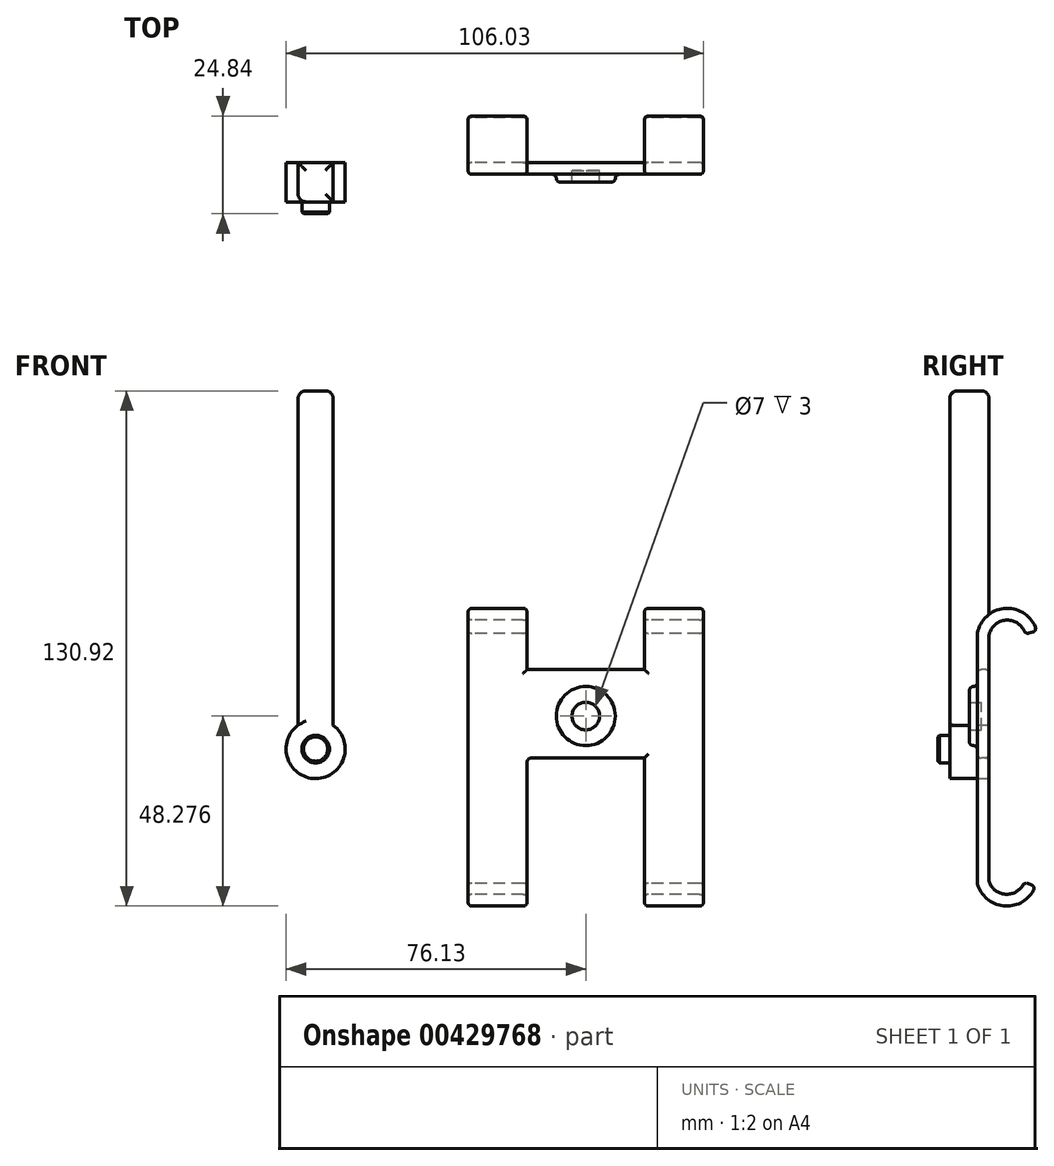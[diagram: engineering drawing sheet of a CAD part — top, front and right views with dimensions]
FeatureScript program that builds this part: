
annotation { "Feature Type Name" : "Feature", "Feature Type Description" : "" }
export const myFeature = defineFeature(function(context is Context, id is Id, definition is map)
    precondition{}
    {
        {
            var Q0;
            Q0=qCreatedBy(makeId("Right.planeOp"),FACE);
            var sketch = newSketch(context, id + "F0", { "sketchPlane" : qUnion([Q0])});
            skLineSegment(sketch, "E0", {"start": v(0, 2.96) * mm, "end": v(0, 65.68) * mm});
            skArc(sketch, "E1", {"start": v(9.23, 65.81) * mm, "mid": v(4.56, 69.36) * mm, "end": v(0, 65.68) * mm});
            skArc(sketch, "E2", {"start": v(0, 2.96) * mm, "mid": v(4.42, -0.3) * mm, "end": v(8.96, 2.78) * mm});
            skPoint(sketch, "E3.orphan", {"position": v(0, 0) * mm});
            skArc(sketch, "E4.0", {"start": v(-3, 2.53) * mm, "mid": v(4.09, -3.29) * mm, "end": v(11.77, 1.72) * mm});
            skLineSegment(sketch, "E4.1", {"start": v(-3, 2.53) * mm, "end": v(-3, 65.99) * mm});
            skArc(sketch, "E4.2", {"start": v(12.13, 66.57) * mm, "mid": v(4.33, 72.35) * mm, "end": v(-3, 65.99) * mm});
            skLineSegment(sketch, "E5", {"start": v(11.77, 1.72) * mm, "end": v(8.96, 2.78) * mm});
            skLineSegment(sketch, "E6", {"start": v(12.13, 66.57) * mm, "end": v(9.23, 65.81) * mm});
            skSolve(sketch);
        }
        {
            var Q0;
            Q0=makeQuery(id+"F0.imprint","IMPRINT",FACE,{"disambiguationData":[TD([[makeQuery(id+"F0.imprint","IMPRINT",EDGE,{"derivedFrom":sQuery(id+"F0.wireOp",EDGE,"E0")}),1.0]])]});
            extrude(context, id + "F1", {"entities" : qUnion([Q0]), "depth" : 15 * mm});
        }
        {
            var Q0;
            Q0=makeQuery(id+"F1.opExtrude","SWEPT_BODY",BODY,{"disambiguationData":[OSD([sQuery(id+"F0.wireOp",EDGE,"E0"),sQuery(id+"F0.wireOp",EDGE,"E1"),sQuery(id+"F0.wireOp",EDGE,"E2"),sQuery(id+"F0.wireOp",EDGE,"E4.0"),sQuery(id+"F0.wireOp",EDGE,"E4.1"),sQuery(id+"F0.wireOp",EDGE,"E4.2"),sQuery(id+"F0.wireOp",EDGE,"E5"),sQuery(id+"F0.wireOp",EDGE,"E6")])]});
            transform(context, id + "F2", {"entities" : qUnion([Q0]), "transformType" : TransformType.TRANSLATION_3D, "dx" : 44.8 * mm, "dy" : 0 * mm, "dz" : 0 * mm, "makeCopy" : true});
        }
        {
            var Q0;
            Q0=makeQuery(id+"F1.opExtrude","CAP_FACE",FACE,{"disambiguationData":[OSD([sQuery(id+"F0.wireOp",EDGE,"E0"),sQuery(id+"F0.wireOp",EDGE,"E1"),sQuery(id+"F0.wireOp",EDGE,"E2"),sQuery(id+"F0.wireOp",EDGE,"E4.0"),sQuery(id+"F0.wireOp",EDGE,"E4.1"),sQuery(id+"F0.wireOp",EDGE,"E4.2"),sQuery(id+"F0.wireOp",EDGE,"E5"),sQuery(id+"F0.wireOp",EDGE,"E6")])],"isStart":false});
            var sketch = newSketch(context, id + "F3", { "sketchPlane" : qUnion([Q0])});
            skLineSegment(sketch, "E7", {"start": v(0, 34.32) * mm, "end": v(-3, 34.32) * mm});
            skLineSegment(sketch, "E8", {"start": v(0, 56.8) * mm, "end": v(-3, 56.8) * mm});
            skSolve(sketch);
        }
        {
            var Q0;
            {var subQ0=sQuery(id+"F3.wireOp",EDGE,"E7");Q0=makeQuery(id+"F3.imprint","IMPRINT",FACE,{"disambiguationData":[TD([[makeQuery(id+"F3.imprint","IMPRINT",EDGE,{"derivedFrom":subQ0}),-1.0]])]});}
            extrude(context, id + "F4", {"entities" : qUnion([Q0]), "operationType" : NewBodyOperationType.ADD, "endBound" : BoundingType.UP_TO_NEXT, "depth" : 25 * mm});
        }
        {
            var Q0;
            {var subQ0=sQuery(id+"F0.wireOp",EDGE,"E4.1");var subQ1=makeQuery(id+"F1.opExtrude","SWEPT_FACE",FACE,{"disambiguationData":[OSD([subQ0])]});Q0=makeQuery(id+"F4.boolean.opBoolean","MERGE",FACE,{"derivedFrom":[subQ1,makeQuery(id+"F2.opPattern","COPY",FACE,{"derivedFrom":subQ1,"instanceName":"1"}),makeQuery(id+"F4.opExtrude","SWEPT_FACE",FACE,{"disambiguationData":[OSD([subQ0])]})]});}
            var sketch = newSketch(context, id + "F5", { "sketchPlane" : qUnion([Q0])});
            skCircle(sketch, "E9", {"center": v(29.9, 44.98) * mm, "radius": 7.5 * mm});
            skCircle(sketch, "E10", {"center": v(29.9, 44.98) * mm, "radius": 3.5 * mm});
            skSolve(sketch);
        }
        {
            var Q0;
            Q0 = qSketchRegion(id + "F5", true);
            extrude(context, id + "F6", {"entities" : qUnion([Q0]), "operationType" : NewBodyOperationType.ADD, "depth" : 2 * mm});
        }
        {
            var Q0;
            Q0=makeQuery(id+"F6.opExtrude","CAP_EDGE",EDGE,{"disambiguationData":[OSD([sQuery(id+"F5.wireOp",EDGE,"E9")])],"isStart":false});
            var Q1;
            Q1=makeQuery(id+"F4.opExtrude","SWEPT_EDGE",EDGE,{"disambiguationData":[OSD([sQuery(id+"F0.wireOp",EDGE,"E4.1"),sQuery(id+"F3.wireOp",EDGE,"E8")])]});
            var Q2;
            Q2=makeQuery(id+"F4.opExtrude","SWEPT_EDGE",EDGE,{"disambiguationData":[OSD([sQuery(id+"F0.wireOp",EDGE,"E4.1"),sQuery(id+"F3.wireOp",EDGE,"E7")])]});
            var Q3;
            {var subQ0=sQuery(id+"F0.wireOp",EDGE,"E4.1");var subQ2=sQuery(id+"F0.wireOp",EDGE,"E4.0");Q3=makeQuery(id+"F4.boolean.opBoolean","SPLIT",EDGE,{"disambiguationData":[TD([makeQuery(id+"F1.opExtrude","SWEPT_FACE",FACE,{"disambiguationData":[OSD([subQ2])]})])],"derivedFrom":makeQuery(id+"F1.opExtrude","CAP_EDGE",EDGE,{"disambiguationData":[OSD([subQ0])],"isStart":false})});}
            var Q4;
            {var subQ0=sQuery(id+"F0.wireOp",EDGE,"E4.1");var subQ2=sQuery(id+"F0.wireOp",EDGE,"E4.0");Q4=makeQuery(id+"F4.boolean.opBoolean","SPLIT",EDGE,{"disambiguationData":[TD([makeQuery(id+"F2.opPattern","COPY",FACE,{"derivedFrom":makeQuery(id+"F1.opExtrude","SWEPT_FACE",FACE,{"disambiguationData":[OSD([subQ2])]}),"instanceName":"1"})])],"derivedFrom":makeQuery(id+"F2.opPattern","COPY",EDGE,{"derivedFrom":makeQuery(id+"F1.opExtrude","CAP_EDGE",EDGE,{"disambiguationData":[OSD([subQ0])],"isStart":true}),"instanceName":"1"})});}
            var Q5;
            {var subQ2=sQuery(id+"F0.wireOp",EDGE,"E4.0");var subQ3=makeQuery(id+"F1.opExtrude","SWEPT_FACE",FACE,{"disambiguationData":[OSD([subQ2])]});var subQ6=sQuery(id+"F0.wireOp",EDGE,"E4.1");var subQ12=makeQuery(id+"F1.opExtrude","SWEPT_FACE",FACE,{"disambiguationData":[OSD([subQ6])]});Q5=makeQuery(id+"F6.boolean.opBoolean","SPLIT",FACE,{"disambiguationData":[TD([subQ3])],"derivedFrom":makeQuery(id+"F4.boolean.opBoolean","MERGE",FACE,{"derivedFrom":[subQ12,makeQuery(id+"F2.opPattern","COPY",FACE,{"derivedFrom":subQ12,"instanceName":"1"}),makeQuery(id+"F4.opExtrude","SWEPT_FACE",FACE,{"disambiguationData":[OSD([subQ6])]})]})});}
            var Q6;
            {var subQ0=sQuery(id+"F0.wireOp",EDGE,"E0");var subQ1=makeQuery(id+"F1.opExtrude","SWEPT_FACE",FACE,{"disambiguationData":[OSD([subQ0])]});Q6=makeQuery(id+"F4.boolean.opBoolean","MERGE",FACE,{"derivedFrom":[subQ1,makeQuery(id+"F2.opPattern","COPY",FACE,{"derivedFrom":subQ1,"instanceName":"1"}),makeQuery(id+"F4.opExtrude","SWEPT_FACE",FACE,{"disambiguationData":[OSD([subQ0])]})]});}
            var Q7;
            Q7=makeQuery(id+"F1.opExtrude","SWEPT_FACE",FACE,{"disambiguationData":[OSD([sQuery(id+"F0.wireOp",EDGE,"E4.0")])]});
            var Q8;
            Q8=makeQuery(id+"F1.opExtrude","SWEPT_FACE",FACE,{"disambiguationData":[OSD([sQuery(id+"F0.wireOp",EDGE,"E4.2")])]});
            var Q9;
            Q9=makeQuery(id+"F2.opPattern","COPY",FACE,{"derivedFrom":makeQuery(id+"F1.opExtrude","SWEPT_FACE",FACE,{"disambiguationData":[OSD([sQuery(id+"F0.wireOp",EDGE,"E4.2")])]}),"instanceName":"1"});
            var Q10;
            Q10=makeQuery(id+"F2.opPattern","COPY",EDGE,{"derivedFrom":makeQuery(id+"F1.opExtrude","SWEPT_EDGE",EDGE,{"disambiguationData":[OSD([sQuery(id+"F0.wireOp",EDGE,"E0"),sQuery(id+"F0.wireOp",EDGE,"E2")])]}),"instanceName":"1"});
            var Q11;
            Q11=makeQuery(id+"F2.opPattern","COPY",EDGE,{"derivedFrom":makeQuery(id+"F1.opExtrude","CAP_EDGE",EDGE,{"disambiguationData":[OSD([sQuery(id+"F0.wireOp",EDGE,"E0")])],"isStart":false}),"instanceName":"1"});
            var Q12;
            Q12=makeQuery(id+"F2.opPattern","COPY",EDGE,{"derivedFrom":makeQuery(id+"F1.opExtrude","CAP_EDGE",EDGE,{"disambiguationData":[OSD([sQuery(id+"F0.wireOp",EDGE,"E2")])],"isStart":true}),"instanceName":"1"});
            var Q13;
            Q13=makeQuery(id+"F2.opPattern","COPY",EDGE,{"derivedFrom":makeQuery(id+"F1.opExtrude","SWEPT_EDGE",EDGE,{"disambiguationData":[OSD([sQuery(id+"F0.wireOp",EDGE,"E4.0"),sQuery(id+"F0.wireOp",EDGE,"E5")])]}),"instanceName":"1"});
            var Q14;
            Q14=makeQuery(id+"F2.opPattern","COPY",EDGE,{"derivedFrom":makeQuery(id+"F1.opExtrude","SWEPT_EDGE",EDGE,{"disambiguationData":[OSD([sQuery(id+"F0.wireOp",EDGE,"E2"),sQuery(id+"F0.wireOp",EDGE,"E5")])]}),"instanceName":"1"});
            var Q15;
            {var subQ0=sQuery(id+"F0.wireOp",EDGE,"E2");var subQ1=sQuery(id+"F0.wireOp",EDGE,"E0");Q15=makeQuery(id+"F4.boolean.opBoolean","SPLIT",EDGE,{"disambiguationData":[TD([makeQuery(id+"F2.opPattern","COPY",FACE,{"derivedFrom":makeQuery(id+"F1.opExtrude","SWEPT_FACE",FACE,{"disambiguationData":[OSD([subQ0])]}),"instanceName":"1"})])],"derivedFrom":makeQuery(id+"F2.opPattern","COPY",EDGE,{"derivedFrom":makeQuery(id+"F1.opExtrude","CAP_EDGE",EDGE,{"disambiguationData":[OSD([subQ1])],"isStart":true}),"instanceName":"1"})});}
            var Q16;
            Q16=makeQuery(id+"F2.opPattern","COPY",EDGE,{"derivedFrom":makeQuery(id+"F1.opExtrude","CAP_EDGE",EDGE,{"disambiguationData":[OSD([sQuery(id+"F0.wireOp",EDGE,"E4.0")])],"isStart":true}),"instanceName":"1"});
            var Q17;
            Q17=makeQuery(id+"F2.opPattern","COPY",EDGE,{"derivedFrom":makeQuery(id+"F1.opExtrude","CAP_EDGE",EDGE,{"disambiguationData":[OSD([sQuery(id+"F0.wireOp",EDGE,"E5")])],"isStart":true}),"instanceName":"1"});
            var Q18;
            Q18=makeQuery(id+"F1.opExtrude","SWEPT_EDGE",EDGE,{"disambiguationData":[OSD([sQuery(id+"F0.wireOp",EDGE,"E4.0"),sQuery(id+"F0.wireOp",EDGE,"E5")])]});
            var Q19;
            Q19=makeQuery(id+"F1.opExtrude","SWEPT_EDGE",EDGE,{"disambiguationData":[OSD([sQuery(id+"F0.wireOp",EDGE,"E4.1"),sQuery(id+"F0.wireOp",EDGE,"E4.2")])]});
            var Q20;
            Q20=makeQuery(id+"F1.opExtrude","CAP_EDGE",EDGE,{"disambiguationData":[OSD([sQuery(id+"F0.wireOp",EDGE,"E1")])],"isStart":false});
            var Q21;
            Q21=makeQuery(id+"F2.opPattern","COPY",EDGE,{"derivedFrom":makeQuery(id+"F1.opExtrude","SWEPT_EDGE",EDGE,{"disambiguationData":[OSD([sQuery(id+"F0.wireOp",EDGE,"E4.0"),sQuery(id+"F0.wireOp",EDGE,"E4.1")])]}),"instanceName":"1"});
            var Q22;
            Q22=makeQuery(id+"F2.opPattern","COPY",EDGE,{"derivedFrom":makeQuery(id+"F1.opExtrude","CAP_EDGE",EDGE,{"disambiguationData":[OSD([sQuery(id+"F0.wireOp",EDGE,"E4.0")])],"isStart":false}),"instanceName":"1"});
            var Q23;
            Q23=makeQuery(id+"F4.opExtrude","SWEPT_EDGE",EDGE,{"disambiguationData":[OSD([sQuery(id+"F0.wireOp",EDGE,"E0"),sQuery(id+"F3.wireOp",EDGE,"E7")])]});
            var Q24;
            Q24=makeQuery(id+"F1.opExtrude","SWEPT_EDGE",EDGE,{"disambiguationData":[OSD([sQuery(id+"F0.wireOp",EDGE,"E4.0"),sQuery(id+"F0.wireOp",EDGE,"E4.1")])]});
            var Q25;
            Q25=makeQuery(id+"F1.opExtrude","SWEPT_EDGE",EDGE,{"disambiguationData":[OSD([sQuery(id+"F0.wireOp",EDGE,"E2"),sQuery(id+"F0.wireOp",EDGE,"E5")])]});
            var Q26;
            Q26=makeQuery(id+"F1.opExtrude","CAP_EDGE",EDGE,{"disambiguationData":[OSD([sQuery(id+"F0.wireOp",EDGE,"E2")])],"isStart":false});
            var Q27;
            Q27=makeQuery(id+"F1.opExtrude","SWEPT_EDGE",EDGE,{"disambiguationData":[OSD([sQuery(id+"F0.wireOp",EDGE,"E4.2"),sQuery(id+"F0.wireOp",EDGE,"E6")])]});
            var Q28;
            Q28=makeQuery(id+"F1.opExtrude","CAP_EDGE",EDGE,{"disambiguationData":[OSD([sQuery(id+"F0.wireOp",EDGE,"E4.0")])],"isStart":true});
            var Q29;
            Q29=makeQuery(id+"F1.opExtrude","CAP_EDGE",EDGE,{"disambiguationData":[OSD([sQuery(id+"F0.wireOp",EDGE,"E4.0")])],"isStart":false});
            var Q30;
            Q30=makeQuery(id+"F1.opExtrude","SWEPT_EDGE",EDGE,{"disambiguationData":[OSD([sQuery(id+"F0.wireOp",EDGE,"E0"),sQuery(id+"F0.wireOp",EDGE,"E2")])]});
            var Q31;
            Q31=makeQuery(id+"F2.opPattern","COPY",EDGE,{"derivedFrom":makeQuery(id+"F1.opExtrude","SWEPT_EDGE",EDGE,{"disambiguationData":[OSD([sQuery(id+"F0.wireOp",EDGE,"E4.2"),sQuery(id+"F0.wireOp",EDGE,"E6")])]}),"instanceName":"1"});
            var Q32;
            Q32=makeQuery(id+"F2.opPattern","COPY",EDGE,{"derivedFrom":makeQuery(id+"F1.opExtrude","SWEPT_EDGE",EDGE,{"disambiguationData":[OSD([sQuery(id+"F0.wireOp",EDGE,"E4.1"),sQuery(id+"F0.wireOp",EDGE,"E4.2")])]}),"instanceName":"1"});
            var Q33;
            Q33=makeQuery(id+"F2.opPattern","COPY",EDGE,{"derivedFrom":makeQuery(id+"F1.opExtrude","SWEPT_EDGE",EDGE,{"disambiguationData":[OSD([sQuery(id+"F0.wireOp",EDGE,"E1"),sQuery(id+"F0.wireOp",EDGE,"E6")])]}),"instanceName":"1"});
            var Q34;
            Q34=makeQuery(id+"F2.opPattern","COPY",EDGE,{"derivedFrom":makeQuery(id+"F1.opExtrude","SWEPT_EDGE",EDGE,{"disambiguationData":[OSD([sQuery(id+"F0.wireOp",EDGE,"E0"),sQuery(id+"F0.wireOp",EDGE,"E1")])]}),"instanceName":"1"});
            var Q35;
            Q35=makeQuery(id+"F2.opPattern","COPY",EDGE,{"derivedFrom":makeQuery(id+"F1.opExtrude","CAP_EDGE",EDGE,{"disambiguationData":[OSD([sQuery(id+"F0.wireOp",EDGE,"E2")])],"isStart":false}),"instanceName":"1"});
            var Q36;
            Q36=makeQuery(id+"F2.opPattern","COPY",EDGE,{"derivedFrom":makeQuery(id+"F1.opExtrude","CAP_EDGE",EDGE,{"disambiguationData":[OSD([sQuery(id+"F0.wireOp",EDGE,"E4.1")])],"isStart":false}),"instanceName":"1"});
            var Q37;
            Q37=makeQuery(id+"F4.opExtrude","SWEPT_EDGE",EDGE,{"disambiguationData":[OSD([sQuery(id+"F0.wireOp",EDGE,"E0"),sQuery(id+"F3.wireOp",EDGE,"E8")])]});
            var Q38;
            Q38=makeQuery(id+"F4.opExtrude","TWEAK_EDGE",EDGE,{"derivedFrom":[makeQuery(id+"F2.opPattern","COPY",FACE,{"derivedFrom":makeQuery(id+"F1.opExtrude","CAP_FACE",FACE,{"disambiguationData":[OSD([sQuery(id+"F0.wireOp",EDGE,"E0"),sQuery(id+"F0.wireOp",EDGE,"E1"),sQuery(id+"F0.wireOp",EDGE,"E2"),sQuery(id+"F0.wireOp",EDGE,"E4.0"),sQuery(id+"F0.wireOp",EDGE,"E4.1"),sQuery(id+"F0.wireOp",EDGE,"E4.2"),sQuery(id+"F0.wireOp",EDGE,"E5"),sQuery(id+"F0.wireOp",EDGE,"E6")])],"isStart":true}),"instanceName":"1"}),makeQuery(id+"F3.imprint","IMPRINT",EDGE,{"derivedFrom":sQuery(id+"F3.wireOp",EDGE,"E7")})]});
            var Q39;
            Q39=makeQuery(id+"F4.opExtrude","CAP_EDGE",EDGE,{"disambiguationData":[OSD([sQuery(id+"F3.wireOp",EDGE,"E8")])],"isStart":true});
            var Q40;
            Q40=makeQuery(id+"F4.opExtrude","CAP_EDGE",EDGE,{"disambiguationData":[OSD([sQuery(id+"F3.wireOp",EDGE,"E7")])],"isStart":true});
            var Q41;
            Q41=makeQuery(id+"F6.opExtrude","CAP_EDGE",EDGE,{"disambiguationData":[OSD([sQuery(id+"F5.wireOp",EDGE,"E9")])],"isStart":true});
            var Q42;
            Q42=makeQuery(id+"F1.opExtrude","SWEPT_EDGE",EDGE,{"disambiguationData":[OSD([sQuery(id+"F0.wireOp",EDGE,"E1"),sQuery(id+"F0.wireOp",EDGE,"E6")])]});
            var Q43;
            {var subQ0=sQuery(id+"F0.wireOp",EDGE,"E0");var subQ2=sQuery(id+"F0.wireOp",EDGE,"E1");Q43=makeQuery(id+"F4.boolean.opBoolean","SPLIT",EDGE,{"disambiguationData":[TD([makeQuery(id+"F1.opExtrude","SWEPT_FACE",FACE,{"disambiguationData":[OSD([subQ2])]})])],"derivedFrom":makeQuery(id+"F1.opExtrude","CAP_EDGE",EDGE,{"disambiguationData":[OSD([subQ0])],"isStart":false})});}
            var Q44;
            Q44=makeQuery(id+"F1.opExtrude","SWEPT_EDGE",EDGE,{"disambiguationData":[OSD([sQuery(id+"F0.wireOp",EDGE,"E0"),sQuery(id+"F0.wireOp",EDGE,"E1")])]});
            var Q45;
            Q45=makeQuery(id+"F1.opExtrude","CAP_EDGE",EDGE,{"disambiguationData":[OSD([sQuery(id+"F0.wireOp",EDGE,"E0")])],"isStart":true});
            var Q46;
            {var subQ0=sQuery(id+"F0.wireOp",EDGE,"E4.1");var subQ2=sQuery(id+"F0.wireOp",EDGE,"E4.2");Q46=makeQuery(id+"F4.boolean.opBoolean","SPLIT",EDGE,{"disambiguationData":[TD([makeQuery(id+"F1.opExtrude","SWEPT_FACE",FACE,{"disambiguationData":[OSD([subQ2])]})])],"derivedFrom":makeQuery(id+"F1.opExtrude","CAP_EDGE",EDGE,{"disambiguationData":[OSD([subQ0])],"isStart":false})});}
            var Q47;
            Q47=makeQuery(id+"F1.opExtrude","CAP_EDGE",EDGE,{"disambiguationData":[OSD([sQuery(id+"F0.wireOp",EDGE,"E1")])],"isStart":true});
            var Q48;
            Q48=makeQuery(id+"F1.opExtrude","CAP_EDGE",EDGE,{"disambiguationData":[OSD([sQuery(id+"F0.wireOp",EDGE,"E2")])],"isStart":true});
            var Q49;
            Q49=makeQuery(id+"F1.opExtrude","CAP_EDGE",EDGE,{"disambiguationData":[OSD([sQuery(id+"F0.wireOp",EDGE,"E4.1")])],"isStart":true});
            var Q50;
            {var subQ0=sQuery(id+"F0.wireOp",EDGE,"E4.2");var subQ1=sQuery(id+"F0.wireOp",EDGE,"E4.1");Q50=makeQuery(id+"F4.boolean.opBoolean","SPLIT",EDGE,{"disambiguationData":[TD([makeQuery(id+"F2.opPattern","COPY",FACE,{"derivedFrom":makeQuery(id+"F1.opExtrude","SWEPT_FACE",FACE,{"disambiguationData":[OSD([subQ0])]}),"instanceName":"1"})])],"derivedFrom":makeQuery(id+"F2.opPattern","COPY",EDGE,{"derivedFrom":makeQuery(id+"F1.opExtrude","CAP_EDGE",EDGE,{"disambiguationData":[OSD([subQ1])],"isStart":true}),"instanceName":"1"})});}
            var Q51;
            Q51=makeQuery(id+"F1.opExtrude","CAP_EDGE",EDGE,{"disambiguationData":[OSD([sQuery(id+"F0.wireOp",EDGE,"E4.2")])],"isStart":true});
            var Q52;
            Q52=makeQuery(id+"F1.opExtrude","CAP_EDGE",EDGE,{"disambiguationData":[OSD([sQuery(id+"F0.wireOp",EDGE,"E4.2")])],"isStart":false});
            var Q53;
            Q53=makeQuery(id+"F1.opExtrude","CAP_EDGE",EDGE,{"disambiguationData":[OSD([sQuery(id+"F0.wireOp",EDGE,"E5")])],"isStart":true});
            var Q54;
            Q54=makeQuery(id+"F1.opExtrude","CAP_EDGE",EDGE,{"disambiguationData":[OSD([sQuery(id+"F0.wireOp",EDGE,"E5")])],"isStart":false});
            var Q55;
            Q55=makeQuery(id+"F1.opExtrude","CAP_EDGE",EDGE,{"disambiguationData":[OSD([sQuery(id+"F0.wireOp",EDGE,"E6")])],"isStart":true});
            var Q56;
            Q56=makeQuery(id+"F1.opExtrude","CAP_EDGE",EDGE,{"disambiguationData":[OSD([sQuery(id+"F0.wireOp",EDGE,"E6")])],"isStart":false});
            var Q57;
            Q57=makeQuery(id+"F2.opPattern","COPY",EDGE,{"derivedFrom":makeQuery(id+"F1.opExtrude","CAP_EDGE",EDGE,{"disambiguationData":[OSD([sQuery(id+"F0.wireOp",EDGE,"E1")])],"isStart":true}),"instanceName":"1"});
            var Q58;
            Q58=makeQuery(id+"F2.opPattern","COPY",EDGE,{"derivedFrom":makeQuery(id+"F1.opExtrude","CAP_EDGE",EDGE,{"disambiguationData":[OSD([sQuery(id+"F0.wireOp",EDGE,"E1")])],"isStart":false}),"instanceName":"1"});
            var Q59;
            Q59=makeQuery(id+"F2.opPattern","COPY",EDGE,{"derivedFrom":makeQuery(id+"F1.opExtrude","CAP_EDGE",EDGE,{"disambiguationData":[OSD([sQuery(id+"F0.wireOp",EDGE,"E4.2")])],"isStart":true}),"instanceName":"1"});
            var Q60;
            Q60=makeQuery(id+"F2.opPattern","COPY",EDGE,{"derivedFrom":makeQuery(id+"F1.opExtrude","CAP_EDGE",EDGE,{"disambiguationData":[OSD([sQuery(id+"F0.wireOp",EDGE,"E4.2")])],"isStart":false}),"instanceName":"1"});
            var Q61;
            Q61=makeQuery(id+"F2.opPattern","COPY",EDGE,{"derivedFrom":makeQuery(id+"F1.opExtrude","CAP_EDGE",EDGE,{"disambiguationData":[OSD([sQuery(id+"F0.wireOp",EDGE,"E5")])],"isStart":false}),"instanceName":"1"});
            var Q62;
            Q62=makeQuery(id+"F2.opPattern","COPY",EDGE,{"derivedFrom":makeQuery(id+"F1.opExtrude","CAP_EDGE",EDGE,{"disambiguationData":[OSD([sQuery(id+"F0.wireOp",EDGE,"E6")])],"isStart":true}),"instanceName":"1"});
            var Q63;
            Q63=makeQuery(id+"F2.opPattern","COPY",EDGE,{"derivedFrom":makeQuery(id+"F1.opExtrude","CAP_EDGE",EDGE,{"disambiguationData":[OSD([sQuery(id+"F0.wireOp",EDGE,"E6")])],"isStart":false}),"instanceName":"1"});
            var Q64;
            Q64=makeQuery(id+"F4.opExtrude","TWEAK_EDGE",EDGE,{"derivedFrom":[makeQuery(id+"F2.opPattern","COPY",FACE,{"derivedFrom":makeQuery(id+"F1.opExtrude","CAP_FACE",FACE,{"disambiguationData":[OSD([sQuery(id+"F0.wireOp",EDGE,"E0"),sQuery(id+"F0.wireOp",EDGE,"E1"),sQuery(id+"F0.wireOp",EDGE,"E2"),sQuery(id+"F0.wireOp",EDGE,"E4.0"),sQuery(id+"F0.wireOp",EDGE,"E4.1"),sQuery(id+"F0.wireOp",EDGE,"E4.2"),sQuery(id+"F0.wireOp",EDGE,"E5"),sQuery(id+"F0.wireOp",EDGE,"E6")])],"isStart":true}),"instanceName":"1"}),makeQuery(id+"F3.imprint","IMPRINT",EDGE,{"derivedFrom":sQuery(id+"F3.wireOp",EDGE,"E8")})]});
            var Q65;
            {var subQ0=sQuery(id+"F0.wireOp",EDGE,"E0");var subQ2=sQuery(id+"F0.wireOp",EDGE,"E2");Q65=makeQuery(id+"F4.boolean.opBoolean","SPLIT",EDGE,{"disambiguationData":[TD([makeQuery(id+"F1.opExtrude","SWEPT_FACE",FACE,{"disambiguationData":[OSD([subQ2])]})])],"derivedFrom":makeQuery(id+"F1.opExtrude","CAP_EDGE",EDGE,{"disambiguationData":[OSD([subQ0])],"isStart":false})});}
            var Q66;
            {var subQ0=sQuery(id+"F0.wireOp",EDGE,"E1");var subQ1=sQuery(id+"F0.wireOp",EDGE,"E0");Q66=makeQuery(id+"F4.boolean.opBoolean","SPLIT",EDGE,{"disambiguationData":[TD([makeQuery(id+"F2.opPattern","COPY",FACE,{"derivedFrom":makeQuery(id+"F1.opExtrude","SWEPT_FACE",FACE,{"disambiguationData":[OSD([subQ0])]}),"instanceName":"1"})])],"derivedFrom":makeQuery(id+"F2.opPattern","COPY",EDGE,{"derivedFrom":makeQuery(id+"F1.opExtrude","CAP_EDGE",EDGE,{"disambiguationData":[OSD([subQ1])],"isStart":true}),"instanceName":"1"})});}
            fillet(context, id + "F7", {"entities" : qUnion([Q0, Q1, Q2, Q3, Q4, Q5, Q6, Q7, Q8, Q9, Q10, Q11, Q12, Q13, Q14, Q15, Q16, Q17, Q18, Q19, Q20, Q21, Q22, Q23, Q24, Q25, Q26, Q27, Q28, Q29, Q30, Q31, Q32, Q33, Q34, Q35, Q36, Q37, Q38, Q39, Q40, Q41, Q42, Q43, Q44, Q45, Q46, Q47, Q48, Q49, Q50, Q51, Q52, Q53, Q54, Q55, Q56, Q57, Q58, Q59, Q60, Q61, Q62, Q63, Q64, Q65, Q66]), "radius" : 1 * mm, "tangentPropagation" : true, "allowEdgeOverflow" : false});
        }
        {
            var Q0;
            {var subQ0=sQuery(id+"F0.wireOp",EDGE,"E4.1");var subQ1=makeQuery(id+"F1.opExtrude","SWEPT_FACE",FACE,{"disambiguationData":[OSD([subQ0])]});Q0=makeQuery(id+"F6.boolean.opBoolean","SPLIT",FACE,{"disambiguationData":[TD([makeQuery(id+"F6.opExtrude","SWEPT_FACE",FACE,{"disambiguationData":[OSD([sQuery(id+"F5.wireOp",EDGE,"E10")])]})])],"derivedFrom":makeQuery(id+"F4.boolean.opBoolean","MERGE",FACE,{"derivedFrom":[subQ1,makeQuery(id+"F2.opPattern","COPY",FACE,{"derivedFrom":subQ1,"instanceName":"1"}),makeQuery(id+"F4.opExtrude","SWEPT_FACE",FACE,{"disambiguationData":[OSD([subQ0])]})]})});}
            extrude(context, id + "F8", {"entities" : qUnion([Q0]), "operationType" : NewBodyOperationType.REMOVE, "oppositeDirection" : true, "depth" : 1 * mm});
        }
        {
            var Q0;
            Q0=qCreatedBy(makeId("Front.planeOp"),FACE);
            var sketch = newSketch(context, id + "F9", { "sketchPlane" : qUnion([Q0])});
            skCircle(sketch, "E11", {"center": v(-38.73, 36.6) * mm, "radius": 7.5 * mm});
            skSolve(sketch);
        }
        {
            var Q0;
            Q0=makeQuery(id+"F9.imprint","IMPRINT",FACE,{"disambiguationData":[TD([[makeQuery(id+"F9.imprint","IMPRINT",EDGE,{"derivedFrom":sQuery(id+"F9.wireOp",EDGE,"E11")}),1.0]])]});
            extrude(context, id + "F10", {"entities" : qUnion([Q0]), "depth" : 10 * mm});
        }
        {
            var Q0;
            Q0=makeQuery(id+"F10.opExtrude","CAP_FACE",FACE,{"disambiguationData":[OSD([sQuery(id+"F9.wireOp",EDGE,"E11")])],"isStart":false});
            var sketch = newSketch(context, id + "F11", { "sketchPlane" : qUnion([Q0])});
            skLineSegment(sketch, "E12", {"start": v(-43.2, 42.62) * mm, "end": v(-34.26, 42.62) * mm});
            skSolve(sketch);
        }
        {
            var Q0;
            {var subQ0=sQuery(id+"F11.wireOp",EDGE,"E12");Q0=makeQuery(id+"F11.imprint","IMPRINT",FACE,{"disambiguationData":[TD([[makeQuery(id+"F11.imprint","IMPRINT",EDGE,{"derivedFrom":subQ0}),1.0]])]});}
            extrude(context, id + "F12", {"entities" : qUnion([Q0]), "operationType" : NewBodyOperationType.REMOVE, "endBound" : BoundingType.UP_TO_NEXT, "oppositeDirection" : true, "depth" : 25 * mm});
        }
        {
            var Q0;
            Q0=makeQuery(id+"F10.opExtrude","CAP_FACE",FACE,{"disambiguationData":[OSD([sQuery(id+"F9.wireOp",EDGE,"E11")])],"isStart":false});
            var sketch = newSketch(context, id + "F13", { "sketchPlane" : qUnion([Q0])});
            skCircle(sketch, "E13", {"center": v(-38.73, 36.6) * mm, "radius": 3.5 * mm});
            skSolve(sketch);
        }
        {
            var Q0;
            Q0=makeQuery(id+"F13.imprint","IMPRINT",FACE,{"disambiguationData":[TD([[makeQuery(id+"F13.imprint","IMPRINT",EDGE,{"derivedFrom":sQuery(id+"F13.wireOp",EDGE,"E13")}),1.0]])]});
            extrude(context, id + "F14", {"entities" : qUnion([Q0]), "operationType" : NewBodyOperationType.ADD, "depth" : 3 * mm});
        }
        {
            var Q0;
            Q0=makeQuery(id+"F14.opExtrude","CAP_EDGE",EDGE,{"disambiguationData":[OSD([sQuery(id+"F13.wireOp",EDGE,"E13")])],"isStart":false});
            chamfer(context, id + "F15", {"entities" : qUnion([Q0]), "width" : .4 * mm, "tangentPropagation" : true});
        }
        {
            var Q0;
            Q0=makeQuery(id+"F12.boolean.opBoolean","COPY",FACE,{"derivedFrom":makeQuery(id+"F12.opExtrude","SWEPT_FACE",FACE,{"disambiguationData":[OSD([sQuery(id+"F11.wireOp",EDGE,"E12")])]})});
            extrude(context, id + "F16", {"entities" : qUnion([Q0]), "operationType" : NewBodyOperationType.ADD, "depth" : 85 * mm});
        }
        {
            var Q0;
            Q0=makeQuery(id+"F16.opExtrude","CAP_FACE",FACE,{"disambiguationData":[OSD([sQuery(id+"F11.wireOp",EDGE,"E12")])],"isStart":false});
            var Q1;
            {var subQ0=sQuery(id+"F11.wireOp",EDGE,"E12");var subQ1=sQuery(id+"F9.wireOp",EDGE,"E11");Q1=makeQuery(id+"F16.opExtrude","CAP_EDGE",EDGE,{"disambiguationData":[OSD([subQ1,subQ0]),TDD([makeQuery(id+"F12.boolean.opBoolean","COPY",EDGE,{"derivedFrom":makeQuery(id+"F12.opExtrude","TWEAK_EDGE",EDGE,{"derivedFrom":[makeQuery(id+"F10.opExtrude","CAP_FACE",FACE,{"disambiguationData":[OSD([subQ1])],"isStart":true}),makeQuery(id+"F11.imprint","IMPRINT",EDGE,{"derivedFrom":subQ0})]})})])],"isStart":false});}
            var Q2;
            {var subQ0=sQuery(id+"F11.wireOp",EDGE,"E12");var subQ1=sQuery(id+"F9.wireOp",EDGE,"E11");Q2=makeQuery(id+"F16.opExtrude","SWEPT_FACE",FACE,{"disambiguationData":[OSD([subQ1,subQ0]),TDD([makeQuery(id+"F12.boolean.opBoolean","COPY",EDGE,{"derivedFrom":makeQuery(id+"F12.opExtrude","SWEPT_EDGE",EDGE,{"disambiguationData":[OSD([subQ1,subQ0]),TDD([makeQuery(id+"F11.imprint","INTERSECT",VERTEX,{"disambiguationData":[OD(0.0)],"derivedFrom":[makeQuery(id+"F10.opExtrude","CAP_EDGE",EDGE,{"disambiguationData":[OSD([subQ1])],"isStart":false}),subQ0]})])]})})])]});}
            var Q3;
            {var subQ0=sQuery(id+"F11.wireOp",EDGE,"E12");var subQ1=sQuery(id+"F9.wireOp",EDGE,"E11");Q3=makeQuery(id+"F16.opExtrude","SWEPT_EDGE",EDGE,{"disambiguationData":[OSD([subQ1,subQ0]),TDD([makeQuery(id+"F12.boolean.opBoolean","COPY",VERTEX,{"derivedFrom":makeQuery(id+"F12.opExtrude","CAP_VERTEX",VERTEX,{"disambiguationData":[OSD([subQ1,subQ0]),TDD([makeQuery(id+"F11.imprint","INTERSECT",VERTEX,{"disambiguationData":[OD(0.0)],"derivedFrom":[makeQuery(id+"F10.opExtrude","CAP_EDGE",EDGE,{"disambiguationData":[OSD([subQ1])],"isStart":false}),subQ0]})])],"isStart":true})})])]});}
            var Q4;
            {var subQ0=sQuery(id+"F11.wireOp",EDGE,"E12");var subQ1=sQuery(id+"F9.wireOp",EDGE,"E11");Q4=makeQuery(id+"F16.opExtrude","SWEPT_FACE",FACE,{"disambiguationData":[OSD([subQ1,subQ0]),TDD([makeQuery(id+"F12.boolean.opBoolean","COPY",EDGE,{"derivedFrom":makeQuery(id+"F12.opExtrude","SWEPT_EDGE",EDGE,{"disambiguationData":[OSD([subQ1,subQ0]),TDD([makeQuery(id+"F11.imprint","INTERSECT",VERTEX,{"disambiguationData":[OD(1.0)],"derivedFrom":[makeQuery(id+"F10.opExtrude","CAP_EDGE",EDGE,{"disambiguationData":[OSD([subQ1])],"isStart":false}),subQ0]})])]})})])]});}
            fillet(context, id + "F17", {"entities" : qUnion([Q0, Q1, Q2, Q3, Q4]), "radius" : 2 * mm, "tangentPropagation" : true, "allowEdgeOverflow" : false});
        }
    });
